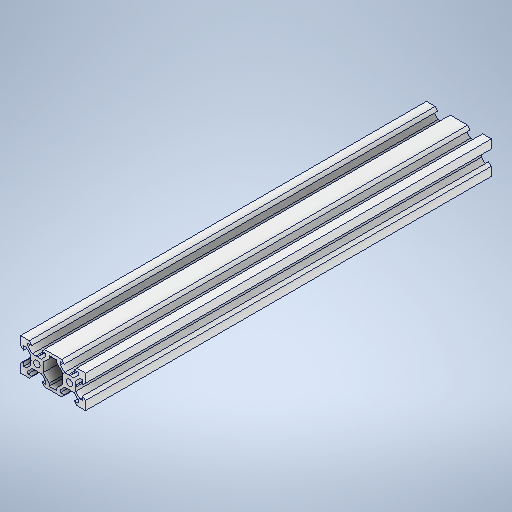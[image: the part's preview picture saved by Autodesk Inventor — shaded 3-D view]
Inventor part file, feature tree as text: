
AUTODESK INVENTOR PART (.ipt)
format: ipt  version: 2025.2 (Build 292293000, 293)  size: 387,072 bytes
history: native  units: in
note: dims shown in document units (in); Inventor stores cm internally (conversion verified against a paired STEP export)
features: plane x2, extrude x1, sketch x1, other x1
ambient origin geometry x8: Origin, YZ Plane, XZ Plane, XY Plane, X Axis, Y Axis, Z Axis, Center Point
bodies: Solid1 (feature_tree)
feature tree (5):
  extrude  "Extrusion1"  [1 undecoded]
  plane  "Work Plane1"
  plane  "Work Plane2"
  sketch  "Sketch1"  dims[d0=9.8425in d1=0.0in]
  other  "Boss-Extrude1"
note: 1 required parameter value undecoded (feature->parameter linkage not recoverable at this tier; creation-order binding heuristic only, values carry confidence <= 0.55)
